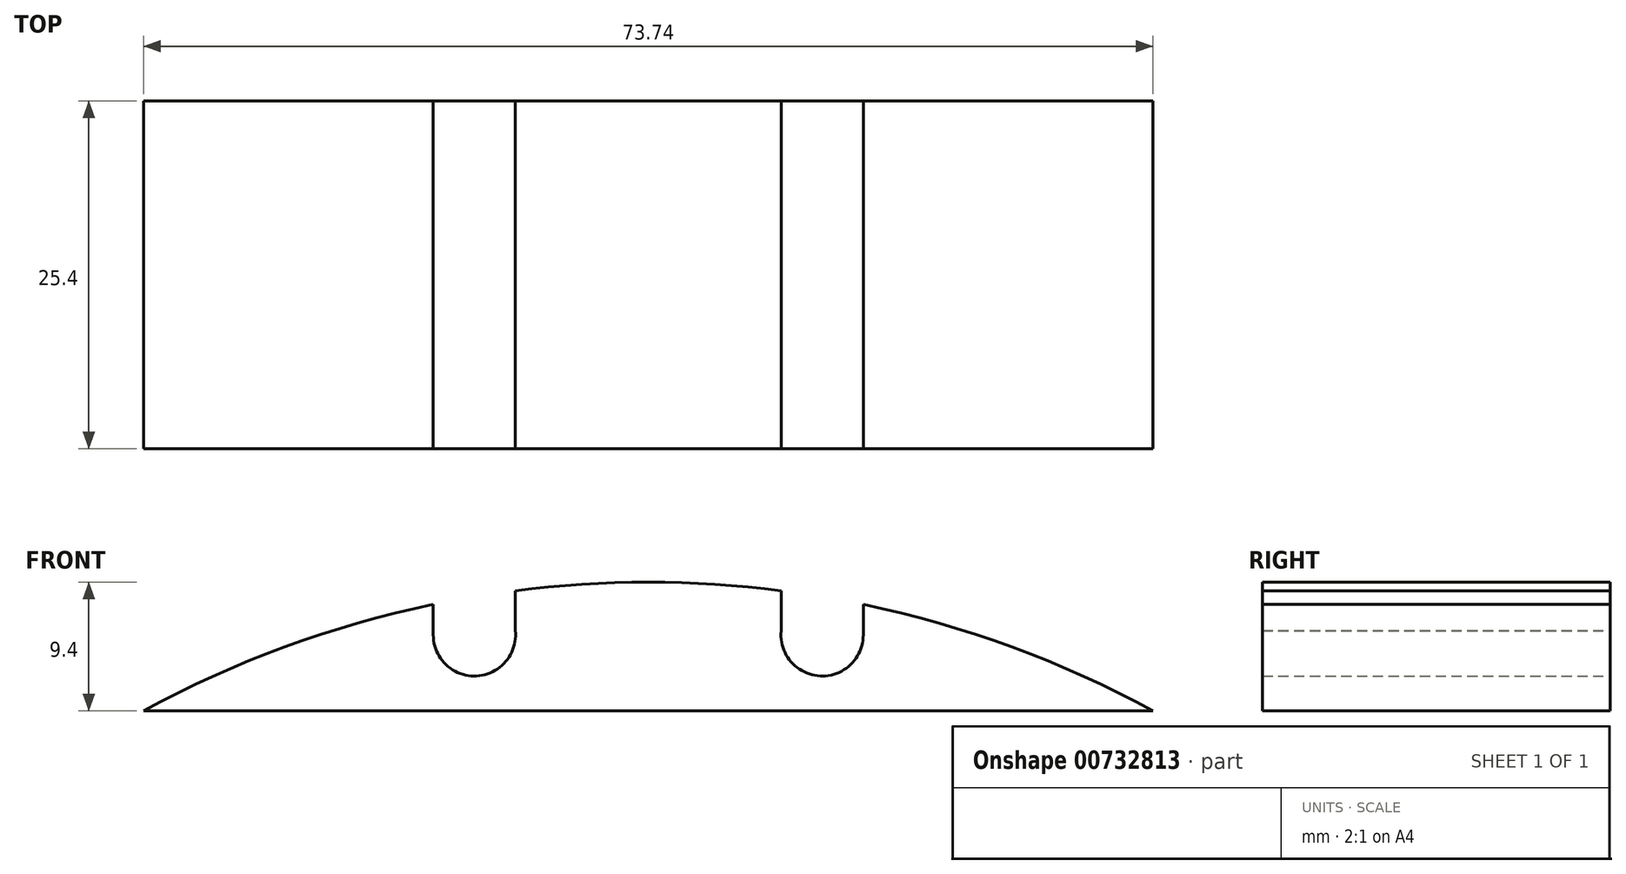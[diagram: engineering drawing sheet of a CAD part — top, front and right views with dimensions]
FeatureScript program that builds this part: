
annotation { "Feature Type Name" : "Feature", "Feature Type Description" : "" }
export const myFeature = defineFeature(function(context is Context, id is Id, definition is map)
    precondition{}
    {
        {
            var Q0;
            Q0=qCreatedBy(makeId("Front.planeOp"),FACE);
            var sketch = newSketch(context, id + "F0", { "sketchPlane" : qUnion([Q0])});
            skCircle(sketch, "E0", {"center": v(0, 0) * mm, "radius": 77.03 * mm});
            skLineSegment(sketch, "E1.bottom", {"start": v(-75.18, 67.63) * mm, "end": v(75.18, 67.63) * mm});
            skLineSegment(sketch, "E1.top", {"start": v(-75.18, -53.33) * mm, "end": v(75.18, -53.33) * mm});
            skLineSegment(sketch, "E1.left", {"start": v(-75.18, 67.63) * mm, "end": v(-75.18, -53.33) * mm});
            skLineSegment(sketch, "E1.right", {"start": v(75.18, 67.63) * mm, "end": v(75.18, -53.33) * mm});
            skCircle(sketch, "E2", {"center": v(-12.7, 73.18) * mm, "radius": 3 * mm});
            skCircle(sketch, "E3", {"center": v(12.7, 73.18) * mm, "radius": 3 * mm});
            skLineSegment(sketch, "E4.bottom", {"start": v(-15.7, 73.18) * mm, "end": v(-9.71, 73.18) * mm});
            skLineSegment(sketch, "E4.top", {"start": v(-15.7, 79.31) * mm, "end": v(-9.71, 79.31) * mm});
            skLineSegment(sketch, "E4.left", {"start": v(-15.7, 73.18) * mm, "end": v(-15.7, 79.31) * mm});
            skLineSegment(sketch, "E4.right", {"start": v(-9.71, 73.18) * mm, "end": v(-9.71, 79.31) * mm});
            skLineSegment(sketch, "E5.bottom", {"start": v(15.7, 73.18) * mm, "end": v(9.7, 73.18) * mm});
            skLineSegment(sketch, "E5.top", {"start": v(15.7, 79.94) * mm, "end": v(9.7, 79.94) * mm});
            skLineSegment(sketch, "E5.left", {"start": v(15.7, 73.18) * mm, "end": v(15.7, 79.94) * mm});
            skLineSegment(sketch, "E5.right", {"start": v(9.7, 73.18) * mm, "end": v(9.7, 79.94) * mm});
            skLineSegment(sketch, "E6.bottom", {"start": v(-50.8, 46.04) * mm, "end": v(50.8, 46.04) * mm});
            skLineSegment(sketch, "E6.top", {"start": v(-50.8, 39.69) * mm, "end": v(50.8, 39.69) * mm});
            skLineSegment(sketch, "E6.left", {"start": v(-50.8, 46.04) * mm, "end": v(-50.8, 39.69) * mm});
            skLineSegment(sketch, "E6.right", {"start": v(50.8, 46.04) * mm, "end": v(50.8, 39.69) * mm});
            skLineSegment(sketch, "E7.bottom", {"start": v(-46.05, 50.8) * mm, "end": v(-39.7, 50.8) * mm});
            skLineSegment(sketch, "E7.top", {"start": v(-46.05, -50.8) * mm, "end": v(-39.7, -50.8) * mm});
            skLineSegment(sketch, "E7.left", {"start": v(-46.05, 50.8) * mm, "end": v(-46.05, -50.8) * mm});
            skLineSegment(sketch, "E7.right", {"start": v(-39.7, 50.8) * mm, "end": v(-39.7, -50.8) * mm});
            skPoint(sketch, "E8", {"position": v(-36.87, 67.63) * mm});
            skPoint(sketch, "E9", {"position": v(36.87, 67.63) * mm});
            skSolve(sketch);
        }
        {
            var Q0;
            {var subQ1=sQuery(id+"F0.wireOp",EDGE,"E0");var subQ12=sQuery(id+"F0.wireOp",EDGE,"E5.left");var subQ15=makeQuery(id+"F0.imprint","INTERSECT",VERTEX,{"derivedFrom":[subQ1,subQ12]});Q0=makeQuery(id+"F0.imprint","IMPRINT",FACE,{"disambiguationData":[TD([[makeQuery(id+"F0.imprint","IMPRINT",EDGE,{"disambiguationData":[TD([[subQ15,1.0]])],"derivedFrom":subQ1}),1.0]])]});}
            extrude(context, id + "F1", {"entities" : qUnion([Q0]), "depth" : 25.4 * mm, "offsetDistance" : 25.4 * mm});
        }
    });
